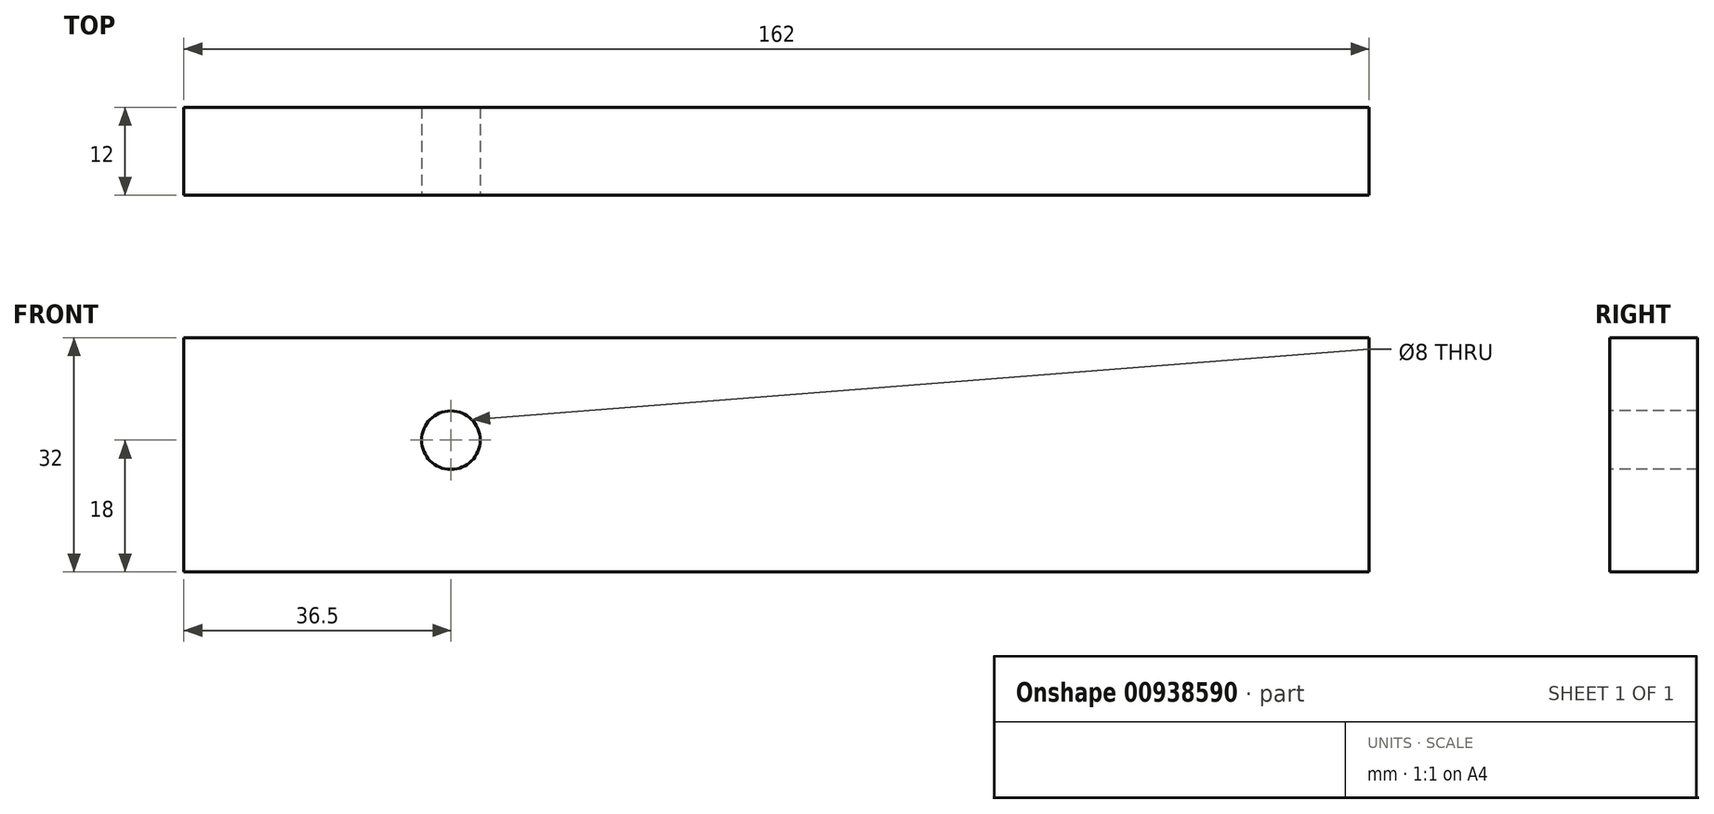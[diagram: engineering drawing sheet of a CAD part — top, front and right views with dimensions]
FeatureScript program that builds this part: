
annotation { "Feature Type Name" : "Feature", "Feature Type Description" : "" }
export const myFeature = defineFeature(function(context is Context, id is Id, definition is map)
    precondition{}
    {
        {
            var Q0;
            Q0=qCreatedBy(makeId("Front.planeOp"),FACE);
            var sketch = newSketch(context, id + "F0", { "sketchPlane" : qUnion([Q0])});
            skLineSegment(sketch, "E0.bottom", {"start": v(81, 16) * mm, "end": v(-81, 16) * mm});
            skLineSegment(sketch, "E0.top", {"start": v(81, -16) * mm, "end": v(-81, -16) * mm});
            skLineSegment(sketch, "E0.left", {"start": v(81, 16) * mm, "end": v(81, -16) * mm});
            skLineSegment(sketch, "E0.right", {"start": v(-81, 16) * mm, "end": v(-81, -16) * mm});
            skPoint(sketch, "E0.middle", {"position": v(0, 0) * mm});
            skSolve(sketch);
        }
        {
            var Q0;
            Q0 = qSketchRegion(id + "F0", true);
            extrude(context, id + "F1", {"entities" : qUnion([Q0]), "oppositeDirection" : true, "depth" : 12 * mm, "offsetDistance" : 25 * mm});
        }
        {
            var Q0;
            Q0=makeQuery(id+"F1.opExtrude","CAP_FACE",FACE,{"disambiguationData":[OSD([sQuery(id+"F0.wireOp",EDGE,"E0.bottom"),sQuery(id+"F0.wireOp",EDGE,"E0.top"),sQuery(id+"F0.wireOp",EDGE,"E0.left"),sQuery(id+"F0.wireOp",EDGE,"E0.right")])],"isStart":true});
            var sketch = newSketch(context, id + "F2", { "sketchPlane" : qUnion([Q0])});
            skLineSegment(sketch, "E1", {"start": v(0, 16) * mm, "end": v(0, -16) * mm, "construction": true});
            skPoint(sketch, "E2", {"position": v(-44.5, 2) * mm});
            skSolve(sketch);
        }
        {
            var Q0;
            Q0=sQuery(id+"F2.wireOp",VERTEX,"E2");
            var Q1;
            Q1=makeQuery(id+"F1.opExtrude","SWEPT_BODY",BODY,{"disambiguationData":[OSD([sQuery(id+"F0.wireOp",EDGE,"E0.bottom"),sQuery(id+"F0.wireOp",EDGE,"E0.top"),sQuery(id+"F0.wireOp",EDGE,"E0.left"),sQuery(id+"F0.wireOp",EDGE,"E0.right")])]});
            hole(context, id + "F3", {"style" : HoleStyle.SIMPLE, "endStyle" : HoleEndStyle.THROUGH, "standardTappedOrClearance" : lookupTablePath({ "standard" : "ISO", "size" : "8", "type" : "Drilled" }), "standardBlindInLast" : lookupTablePath({ "standard" : "ISO", "size" : "8", "type" : "Drilled" }), "holeDiameter" : 8 * mm, "majorDiameter" : 4 * mm, "tappedDepth" : 11.9 * mm, "tapClearance" : 3, "locations" : qUnion([Q0]), "scope" : qUnion([Q1])});
        }
    });
